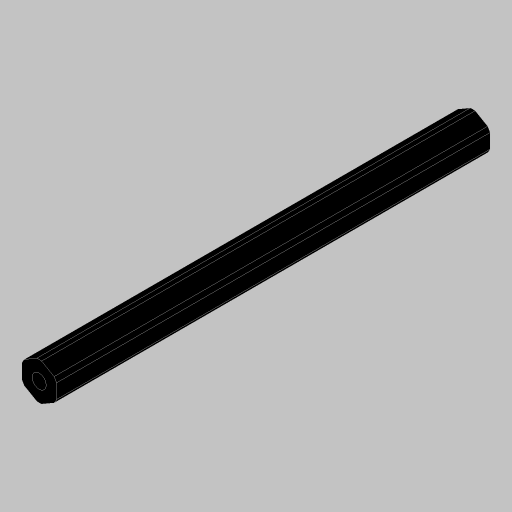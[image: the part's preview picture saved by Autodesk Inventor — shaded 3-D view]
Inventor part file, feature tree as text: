
AUTODESK INVENTOR PART (.ipt)
format: ipt  version: 2023.5 (Build 275446000, 446)  size: 116,224 bytes
history: native  units: in
note: dims shown in document units (in); Inventor stores cm internally (conversion verified against a paired STEP export)
features: extrude x2, projected_geometry x2, hole x1
ambient origin geometry x8: Origin, YZ Plane, XZ Plane, XY Plane, X Axis, Y Axis, Z Axis, Center Point
bodies: Solid1 (feature_tree)
feature tree (5):
  extrude  "Extrusion1"  TaperAngle=0.0deg  [1 undecoded]
  hole  "Hole1"  [1 undecoded]
  extrude  "Extrusion3"  TaperAngle=0.0deg  [1 undecoded]
  projected_geometry  "Project Cut Edges1"
  projected_geometry  "Project Cut Edges2"
note: 3 required parameter values undecoded (feature->parameter linkage not recoverable at this tier; creation-order binding heuristic only, values carry confidence <= 0.55)
